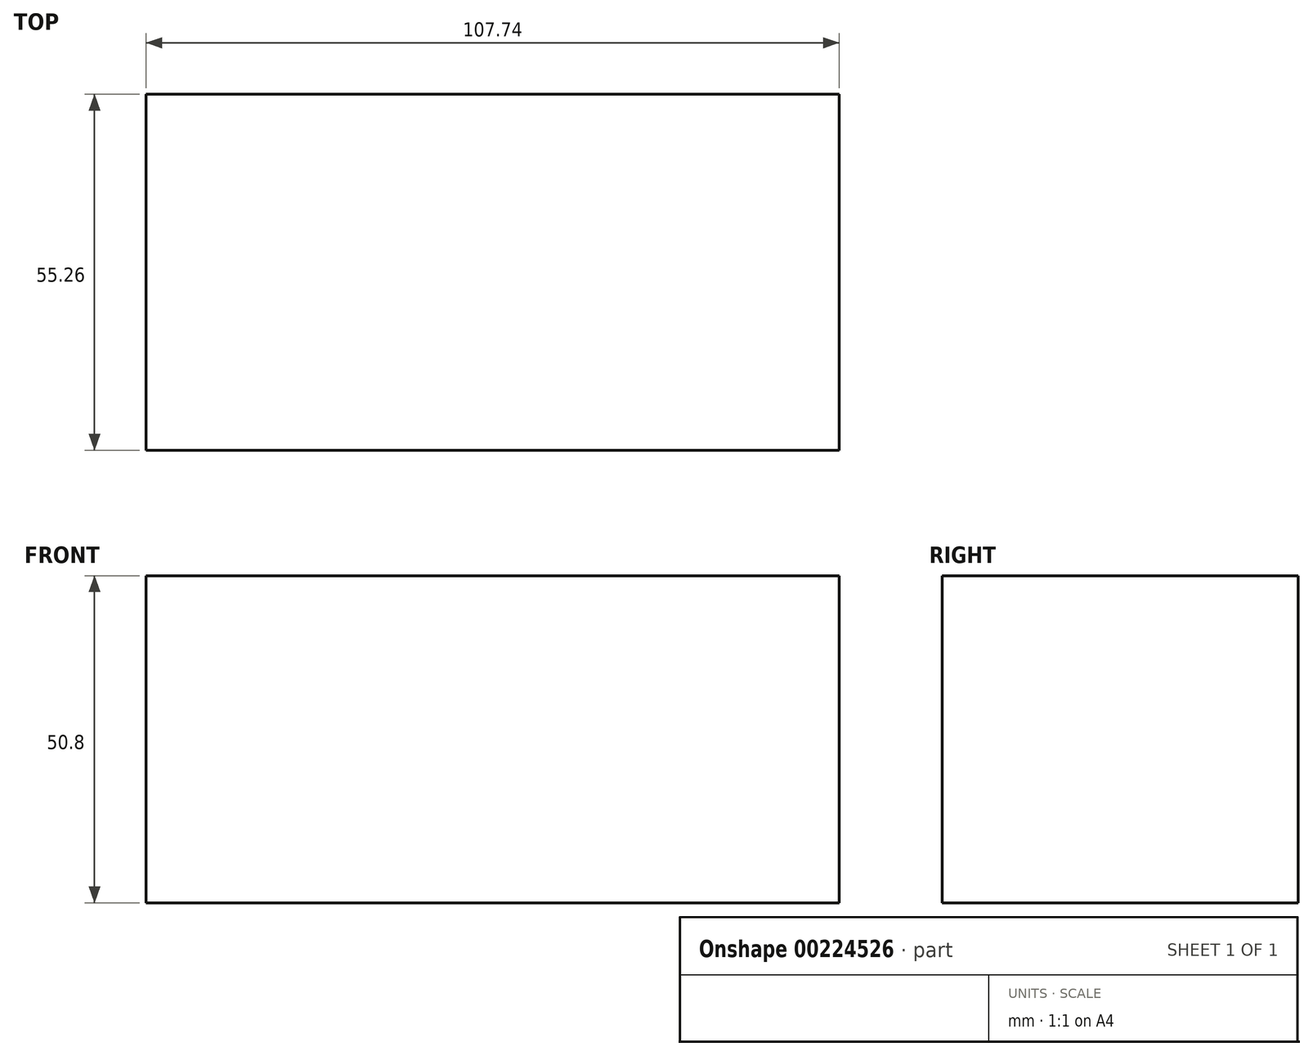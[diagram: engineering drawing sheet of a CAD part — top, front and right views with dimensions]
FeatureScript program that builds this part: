
annotation { "Feature Type Name" : "Feature", "Feature Type Description" : "" }
export const myFeature = defineFeature(function(context is Context, id is Id, definition is map)
    precondition{}
    {
        {
            var Q0;
            Q0=qCreatedBy(makeId("Top.planeOp"),FACE);
            var sketch = newSketch(context, id + "F0", { "sketchPlane" : qUnion([Q0])});
            skLineSegment(sketch, "E0.bottom", {"start": v(-53.87, 27.63) * mm, "end": v(53.87, 27.63) * mm});
            skLineSegment(sketch, "E0.top", {"start": v(-53.87, -27.63) * mm, "end": v(53.87, -27.63) * mm});
            skLineSegment(sketch, "E0.left", {"start": v(-53.87, 27.63) * mm, "end": v(-53.87, -27.63) * mm});
            skLineSegment(sketch, "E0.right", {"start": v(53.87, 27.63) * mm, "end": v(53.87, -27.63) * mm});
            skPoint(sketch, "E0.middle", {"position": v(0, 0) * mm});
            skSolve(sketch);
        }
        {
            var Q0;
            Q0=makeQuery(id+"F0.imprint","IMPRINT",FACE,{"disambiguationData":[TD([[makeQuery(id+"F0.imprint","IMPRINT",EDGE,{"derivedFrom":sQuery(id+"F0.wireOp",EDGE,"E0.bottom")}),-1.0]])]});
            extrude(context, id + "F1", {"entities" : qUnion([Q0]), "depth" : 50.8 * mm});
        }
    });
